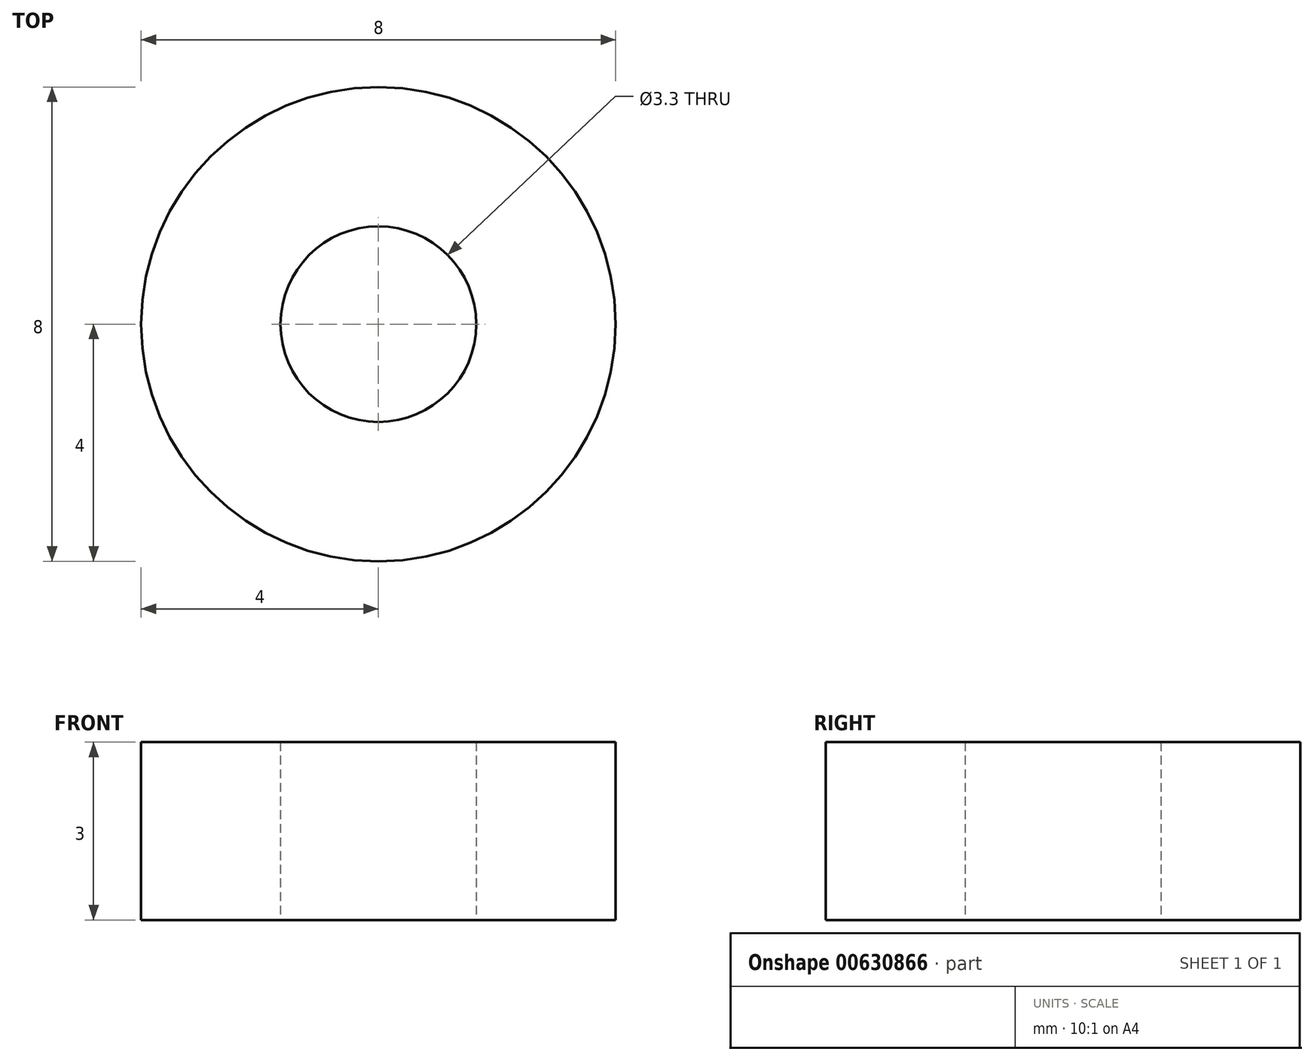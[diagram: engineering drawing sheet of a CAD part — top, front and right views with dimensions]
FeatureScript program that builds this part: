
annotation { "Feature Type Name" : "Feature", "Feature Type Description" : "" }
export const myFeature = defineFeature(function(context is Context, id is Id, definition is map)
    precondition{}
    {
        {
            var Q0;
            Q0=qCreatedBy(makeId("Top.planeOp"),FACE);
            var sketch = newSketch(context, id + "F0", { "sketchPlane" : qUnion([Q0])});
            skCircle(sketch, "E0", {"center": v(0, 0) * mm, "radius": 4 * mm});
            skCircle(sketch, "E1", {"center": v(0, 0) * mm, "radius": 1.65 * mm});
            skSolve(sketch);
        }
        {
            var Q0;
            Q0 = qSketchRegion(id + "F0", true);
            extrude(context, id + "F1", {"entities" : qUnion([Q0]), "depth" : 3 * mm, "offsetDistance" : 25 * mm});
        }
    });
